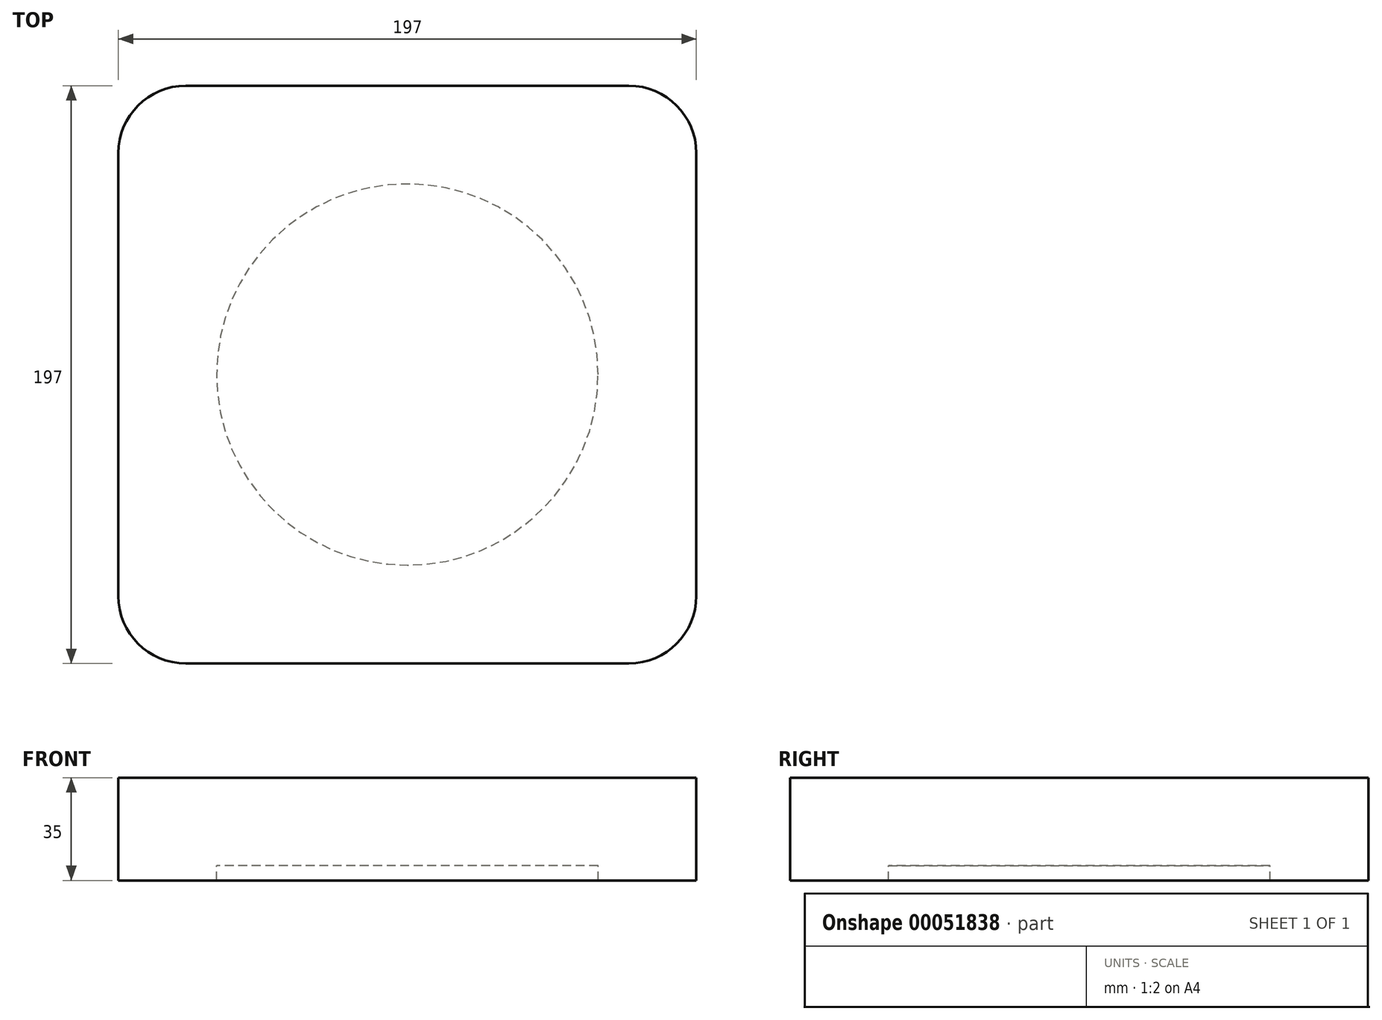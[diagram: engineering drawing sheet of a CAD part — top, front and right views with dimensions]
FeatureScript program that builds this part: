
annotation { "Feature Type Name" : "Feature", "Feature Type Description" : "" }
export const myFeature = defineFeature(function(context is Context, id is Id, definition is map)
    precondition{}
    {
        {
            var Q0;
            Q0=qCreatedBy(makeId("Top.planeOp"),FACE);
            var sketch = newSketch(context, id + "F0", { "sketchPlane" : qUnion([Q0])});
            skLineSegment(sketch, "E0.rect.bottom", {"start": v(75.5, 98.5) * mm, "end": v(-75.5, 98.5) * mm});
            skLineSegment(sketch, "E0.rect.top", {"start": v(75.5, -98.5) * mm, "end": v(-75.5, -98.5) * mm});
            skLineSegment(sketch, "E0.rect.left", {"start": v(98.5, 75.5) * mm, "end": v(98.5, -75.5) * mm});
            skLineSegment(sketch, "E0.rect.right", {"start": v(-98.5, 75.5) * mm, "end": v(-98.5, -75.5) * mm});
            skPoint(sketch, "E0.rect.middle", {"position": v(0, 0) * mm});
            skPoint(sketch, "E1.visualSharp", {"position": v(98.5, 98.5) * mm});
            skArc(sketch, "E1.filletArc", {"start": v(98.5, 75.5) * mm, "mid": v(91.76, 91.76) * mm, "end": v(75.5, 98.5) * mm});
            skPoint(sketch, "E2.visualSharp", {"position": v(-98.5, 98.5) * mm});
            skArc(sketch, "E2.filletArc", {"start": v(-75.5, 98.5) * mm, "mid": v(-91.76, 91.76) * mm, "end": v(-98.5, 75.5) * mm});
            skPoint(sketch, "E3.visualSharp", {"position": v(-98.5, -98.5) * mm});
            skArc(sketch, "E3.filletArc", {"start": v(-98.5, -75.5) * mm, "mid": v(-91.76, -91.76) * mm, "end": v(-75.5, -98.5) * mm});
            skPoint(sketch, "E4.visualSharp", {"position": v(98.5, -98.5) * mm});
            skArc(sketch, "E4.filletArc", {"start": v(75.5, -98.5) * mm, "mid": v(91.76, -91.76) * mm, "end": v(98.5, -75.5) * mm});
            skSolve(sketch);
        }
        {
            var Q0;
            Q0=makeQuery(id+"F0.imprint","IMPRINT",FACE,{"disambiguationData":[TD([[makeQuery(id+"F0.imprint","IMPRINT",EDGE,{"derivedFrom":sQuery(id+"F0.wireOp",EDGE,"E0.rect.bottom")}),1.0]])]});
            extrude(context, id + "F1", {"entities" : qUnion([Q0]), "depth" : 30 * mm});
        }
        {
            var Q0;
            Q0=makeQuery(id+"F0.imprint","IMPRINT",FACE,{"disambiguationData":[TD([[makeQuery(id+"F0.imprint","IMPRINT",EDGE,{"derivedFrom":sQuery(id+"F0.wireOp",EDGE,"E0.rect.bottom")}),1.0]])]});
            var sketch = newSketch(context, id + "F2", { "sketchPlane" : qUnion([Q0])});
            skCircle(sketch, "E5", {"center": v(0, 0) * mm, "radius": 75 * mm});
            skCircle(sketch, "E6", {"center": v(0, 0) * mm, "radius": 65 * mm});
            skCircle(sketch, "E7", {"center": v(0, 0) * mm, "radius": 60 * mm});
            skSolve(sketch);
        }
        {
            var Q0;
            Q0=makeQuery(id+"F2.imprint","IMPRINT",FACE,{"disambiguationData":[TD([[makeQuery(id+"F2.imprint","IMPRINT",EDGE,{"derivedFrom":sQuery(id+"F2.wireOp",EDGE,"E5")}),-1.0]])]});
            var Q1;
            Q1=makeQuery(id+"F2.imprint","IMPRINT",FACE,{"disambiguationData":[TD([[makeQuery(id+"F2.imprint","IMPRINT",EDGE,{"derivedFrom":sQuery(id+"F2.wireOp",EDGE,"E5")}),1.0]])]});
            extrude(context, id + "F3", {"entities" : qUnion([Q0, Q1]), "operationType" : NewBodyOperationType.ADD, "oppositeDirection" : true, "depth" : 5 * mm});
        }
    });
